# Revit family: 1ICON2_RT_24V_In-wall_RFA
name_source: partatom
category: Data Devices
units: mm (PartAtom-declared; Revit-internal decimal feet)

## family parameters
Cut with Voids When Loaded = No
Host = Face
Maintain Annotation Orientation = Yes
Part Type = Normal
Room Calculation Point = No
Round Connector Dimension = Use Diameter
Shared = No

## types (2) — shared parameters
Body Material = Danfoss Plastic White
Description = Main Controller and Room Thermostat
IP Rating = IP 21
IfcExportAs = IfcElectricApplianceType
IfcExportType = ICON2_RT_24V
KR = 15 mm  [stored 0.0492126 ft]
KR1 = 15 mm  [stored 0.0492126 ft]
KR2 = 13 mm
KR3 = 11 mm  [stored 0.0360892 ft]
LOD 200 = No
LOD 350 = Yes
Manufacturer = Danfoss
Power = 0 VA
Power Consumption = 0.2 W
Power Supply = 24 VDC
RN = 2 mm  [stored 0.00656168 ft]
RN1 = 4 mm  [stored 0.0131234 ft]
SketchPlaneIDs = 10482;153b746f-b00a-47b6-946a-48530699bbd5-000028f2
URL = https://store.danfoss.com
Voltage = 24 V
W1 = 6 mm  [stored 0.019685 ft]
W1__ve = -6 mm  [stored -0.019685 ft]
WB = 5 mm  [stored 0.0164042 ft]
WW = 10 mm  [stored 0.0328084 ft]
X1 = 26 mm
XS = 25 mm  [stored 0.082021 ft]
XZ = 20 mm  [stored 0.0656168 ft]
Z1 = 25 mm  [stored 0.082021 ft]
Z2 = 24 mm  [stored 0.0787402 ft]
zero-valued in all types: Default Elevation, L2D, W2D

## per-type parameters (varying)
| type | BP | H | H2 | L | L2 | Model | Model Type |
| Icon2_RT_24V_In-wall_86x86_088U2126 | 80 mm  [stored 0.262467 ft] | 86 mm | 43 mm  [stored 0.141076 ft] | 86 mm | 43 mm  [stored 0.141076 ft] | 088U2126 | Icon2_RT_24V_In-wall_86x86 |
| Icon2_RT_24V_In-wall_80x80_088U2125 | 71 mm | 80 mm  [stored 0.262467 ft] | 40 mm  [stored 0.131234 ft] | 80 mm  [stored 0.262467 ft] | 40 mm  [stored 0.131234 ft] | 088U2125 | Icon2_RT_24V_In-wall_80x80 |

note: [stored X ft] marks values corroborated as IEEE doubles in the binary element streams (Revit-internal decimal feet)

## geometry (parser evidence)
native form markers: Sweep x2
no freeform markers — native parametric forms only
